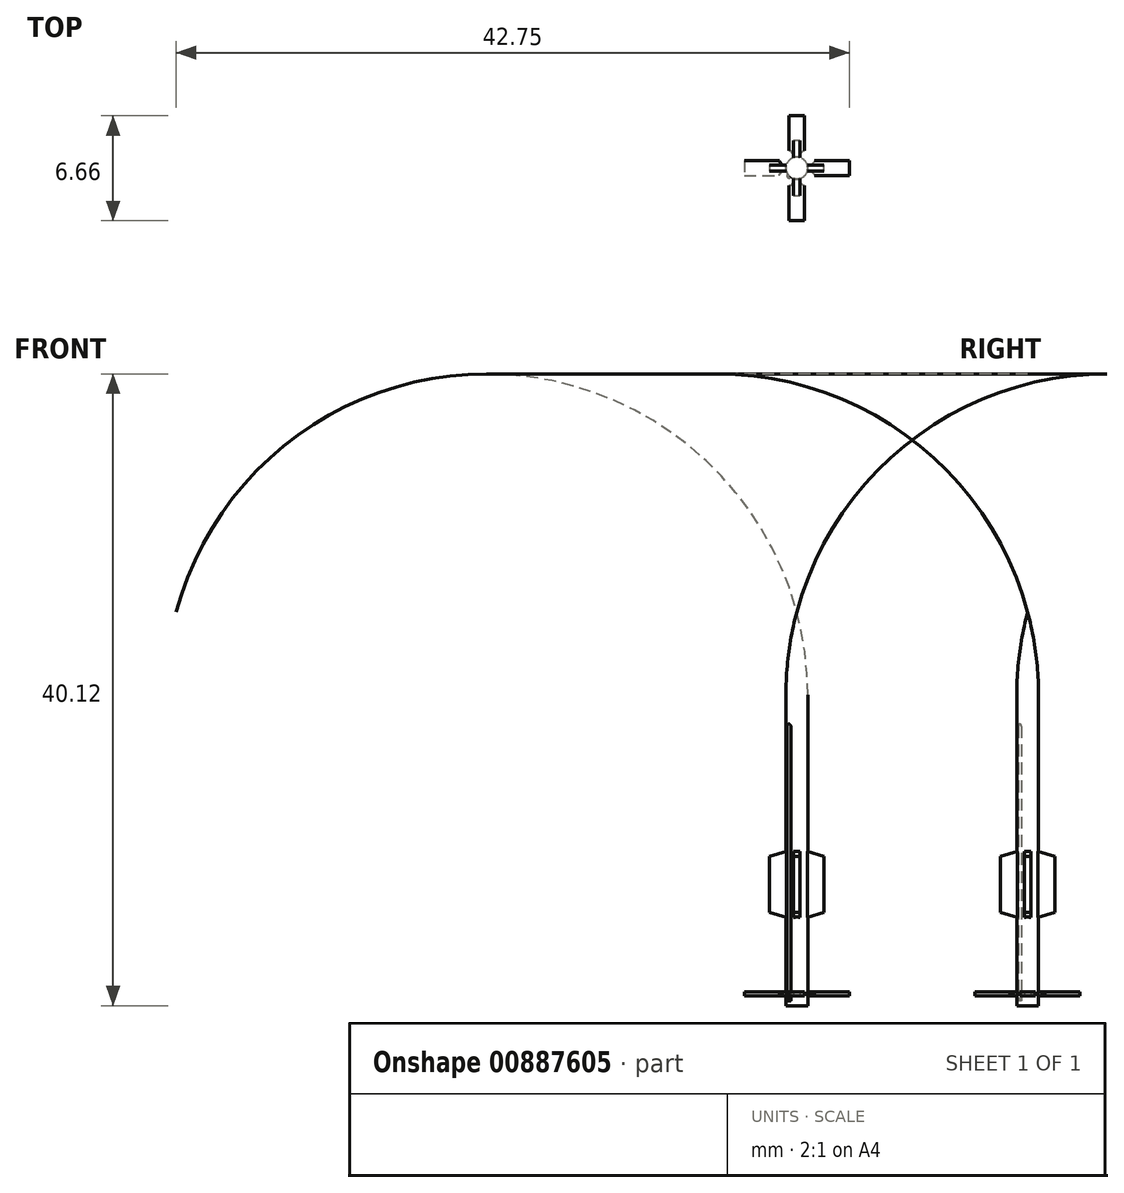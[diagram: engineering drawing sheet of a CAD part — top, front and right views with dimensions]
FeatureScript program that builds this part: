
annotation { "Feature Type Name" : "Feature", "Feature Type Description" : "" }
export const myFeature = defineFeature(function(context is Context, id is Id, definition is map)
    precondition{}
    {
        {
            assignVariable(context, id + "F0", {"name" : "s", "anyValue" : 144});
        }
        {
            var Q0;
            Q0=qCreatedBy(makeId("Front.planeOp"),FACE);
            var sketch = newSketch(context, id + "F1", { "sketchPlane" : qUnion([Q0])});
            skLineSegment(sketch, "E0", {"start": v(0, 0) * mm, "end": v(0, 25) * mm});
            skLineSegment(sketch, "E1", {"start": v(0.7, 19.72) * mm, "end": v(0.7, 0) * mm});
            skLineSegment(sketch, "E2", {"start": v(0.7, 0) * mm, "end": v(0, 0) * mm});
            skArc(sketch, "E3", {"start": v(0.7, 19.72) * mm, "mid": v(0.52, 22.38) * mm, "end": v(0, 25) * mm});
            skSolve(sketch);
        }
        {
            var Q0;
            {var subQ0=sQuery(id+"F1.wireOp",EDGE,"mrwio9nY-PsAZ-Zbfy-NhIU-sYq0QVbgGXAG");Q0=makeQuery(id+"F1.imprint","IMPRINT",FACE,{"disambiguationData":[TD([[makeQuery(id+"F1.imprint","IMPRINT",EDGE,{"derivedFrom":subQ0}),-1.0]])]});}
            var Q1;
            {var subQ7=sQuery(id+"F1.wireOp",EDGE,"E0");Q1=makeQuery(id+"F1.imprint","IMPRINT",FACE,{"disambiguationData":[TD([[makeQuery(id+"F1.imprint","IMPRINT",EDGE,{"derivedFrom":subQ7}),-1.0]])]});}
            var Q2;
            Q2=sQuery(id+"F1.wireOp",EDGE,"E0");
            revolve(context, id + "F2", {"surfaceOperationType" : NewSurfaceOperationType.NEW, "entities" : qUnion([Q0, Q1]), "axis" : qUnion([Q2]), "revolveType" : RevolveType.FULL});
        }
        {
            var Q0;
            Q0=qCreatedBy(makeId("Front.planeOp"),FACE);
            var sketch = newSketch(context, id + "F3", { "sketchPlane" : qUnion([Q0])});
            skLineSegment(sketch, "E4", {"start": v(0, 0) * mm, "end": v(0, 10) * mm});
            skLineSegment(sketch, "E5", {"start": v(0.4, 5.54) * mm, "end": v(0.4, 0.87) * mm});
            skLineSegment(sketch, "E6", {"start": v(0.4, 0.87) * mm, "end": v(3.33, 0.87) * mm});
            skLineSegment(sketch, "E7", {"start": v(3.33, 0.87) * mm, "end": v(3.33, 0.63) * mm});
            skLineSegment(sketch, "E8", {"start": v(0.7, 0) * mm, "end": v(0.7, 32.87) * mm, "construction": true});
            skPoint(sketch, "E9", {"position": v(0.7, 0.87) * mm});
            skLineSegment(sketch, "E10", {"start": v(3.33, 0.63) * mm, "end": v(0, 0.62) * mm});
            skLineSegment(sketch, "E11.0", {"start": v(0.7, 0) * mm, "end": v(-0.7, 0) * mm});
            skLineSegment(sketch, "E12", {"start": v(0.4, 5.54) * mm, "end": v(1.74, 5.94) * mm});
            skLineSegment(sketch, "E13", {"start": v(1.74, 5.94) * mm, "end": v(1.74, 9.48) * mm});
            skLineSegment(sketch, "E14", {"start": v(1.74, 9.48) * mm, "end": v(0, 10) * mm});
            skPoint(sketch, "E15", {"position": v(0.7, 5.62) * mm});
            skPoint(sketch, "E16", {"position": v(0.7, 9.8) * mm});
            skSolve(sketch);
        }
        {
            var Q0;
            Q0=qSketchRegion(id+"F3",true);
            extrude(context, id + "F4", {"entities" : qUnion([Q0]), "operationType" : NewBodyOperationType.ADD, "depth" : .4 * mm, "offsetDistance" : 25 * mm, "symmetric" : true});
        }
        {
            var Q0;
            Q0=makeQuery(id+"F4.opExtrude","SWEPT_FACE",FACE,{"disambiguationData":[OSD([sQuery(id+"F3.wireOp",EDGE,"E10")])]});
            var Q1;
            Q1=makeQuery(id+"F4.opExtrude","SWEPT_FACE",FACE,{"disambiguationData":[OSD([sQuery(id+"F3.wireOp",EDGE,"E10")])]});
            var sketch = newSketch(context, id + "F5", { "sketchPlane" : qUnion([Q0, Q1])});
            skLineSegment(sketch, "E17.bottom", {"start": v(3.33, -0.49) * mm, "end": v(1.11, -0.49) * mm});
            skLineSegment(sketch, "E17.top", {"start": v(3.33, 0.49) * mm, "end": v(1.11, 0.49) * mm});
            skLineSegment(sketch, "E17.left", {"start": v(3.33, -0.49) * mm, "end": v(3.33, 0.49) * mm});
            skLineSegment(sketch, "E17.right", {"start": v(1.11, -0.49) * mm, "end": v(1.11, 0.49) * mm});
            skLineSegment(sketch, "E18", {"start": v(0, 0) * mm, "end": v(1.11, 0) * mm});
            skSolve(sketch);
        }
        {
            var Q0;
            Q0 = qSketchRegion(id + "F5", true);
            var Q1;
            Q1=makeQuery(id+"F4.opExtrude","SWEPT_FACE",FACE,{"disambiguationData":[OSD([sQuery(id+"F3.wireOp",EDGE,"E6")])]});
            extrude(context, id + "F6", {"entities" : qUnion([Q0]), "operationType" : NewBodyOperationType.ADD, "endBound" : BoundingType.UP_TO_SURFACE, "oppositeDirection" : true, "depth" : 25 * mm, "endBoundEntityFace" : qUnion([Q1]), "offsetDistance" : 25 * mm});
        }
        {
            var Q0;
            Q0=makeQuery(id+"F2.opRevolve","SWEPT_BODY",BODY,{"disambiguationData":[OSD([sQuery(id+"F1.wireOp",EDGE,"E0"),sQuery(id+"F1.wireOp",EDGE,"E1"),sQuery(id+"F1.wireOp",EDGE,"E2"),sQuery(id+"F1.wireOp",EDGE,"2EiOItwe-9FNA-eY8p-DkXH-AMy5AHyUmzZA"),sQuery(id+"F1.wireOp",EDGE,"E3")])]});
            var Q1;
            Q1=makeQuery(id+"F2.opRevolve","SWEPT_FACE",FACE,{"disambiguationData":[OSD([sQuery(id+"F1.wireOp",EDGE,"E1")])]});
            circularPattern(context, id + "F7", {"operationType" : NewBodyOperationType.ADD, "entities" : qUnion([Q0]), "axis" : qUnion([Q1]), "angle" : 360 * degree, "instanceCount" : 4, "equalSpace" : true, "computeTransformsWithoutBuiltin" : true});
        }
        {
            var Q0;
            Q0=qCreatedBy(makeId("Top.planeOp"),FACE);
            cPlane(context, id + "F8", {"entities" : qUnion([Q0]), "cplaneType" : CPlaneType.OFFSET, "offset" : (75 / getVariable(context, 's')) * mm, "width" : 150 * mm, "height" : 150 * mm});
        }
        {
            var Q0;
            Q0=qCreatedBy(id+"F8.planeOp",FACE);
            var sketch = newSketch(context, id + "F9", { "sketchPlane" : qUnion([Q0])});
            skLineSegment(sketch, "E19", {"start": v(-0.06, -0.25) * mm, "end": v(-0.25, -0.06) * mm});
            skLineSegment(sketch, "E20", {"start": v(-0.25, -0.06) * mm, "end": v(-0.59, -0.4) * mm});
            skLineSegment(sketch, "E21", {"start": v(-0.4, -0.59) * mm, "end": v(-0.06, -0.25) * mm});
            skLineSegment(sketch, "E22", {"start": v(0, -0.45) * mm, "end": v(0, 0) * mm, "construction": true});
            skLineSegment(sketch, "E23", {"start": v(0, 0) * mm, "end": v(-0.16, -0.16) * mm, "construction": true});
            skArc(sketch, "E24", {"start": v(-0.59, -0.4) * mm, "mid": v(-0.59, -0.59) * mm, "end": v(-0.4, -0.59) * mm});
            skSolve(sketch);
        }
        {
            var Q0;
            Q0=qSketchRegion(id+"F9",true);
            extrude(context, id + "F10", {"entities" : qUnion([Q0]), "operationType" : NewBodyOperationType.ADD, "depth" : (2500 / getVariable(context, 's')) * mm, "offsetDistance" : 25 * mm});
        }
        {
            var Q0;
            Q0=makeQuery(id+"F10.boolean.opBoolean","INTERSECT",EDGE,{"derivedFrom":[makeQuery(id+"F2.opRevolve","SWEPT_FACE",FACE,{"disambiguationData":[OSD([sQuery(id+"F1.wireOp",EDGE,"E1")])]}),makeQuery(id+"F10.opExtrude","CAP_FACE",FACE,{"disambiguationData":[OSD([sQuery(id+"F9.wireOp",EDGE,"E19"),sQuery(id+"F9.wireOp",EDGE,"E20"),sQuery(id+"F9.wireOp",EDGE,"E21"),sQuery(id+"F9.wireOp",EDGE,"E24")])],"isStart":true})]});
            chamfer(context, id + "F11", {"entities" : qUnion([Q0]), "width" : .2 * mm, "tangentPropagation" : true});
        }
        {
            var Q0;
            Q0=makeQuery(id+"F10.opExtrude","CAP_EDGE",EDGE,{"disambiguationData":[OSD([sQuery(id+"F9.wireOp",EDGE,"E24")])],"isStart":false});
            fillet(context, id + "F12", {"entities" : qUnion([Q0]), "radius" : (20 / getVariable(context, 's')) * mm, "tangentPropagation" : true, "allowEdgeOverflow" : false});
        }
        {
            var Q0;
            {var subQ0=sQuery(id+"F3.wireOp",EDGE,"E6");var subQ1=sQuery(id+"F3.wireOp",EDGE,"E7");var subQ2=sQuery(id+"F3.wireOp",EDGE,"E10");Q0=makeQuery(id+"F6.boolean.opBoolean","INTERSECT",EDGE,{"derivedFrom":[makeQuery(id+"F4.boolean.opBoolean","SPLIT",FACE,{"disambiguationData":[TD([makeQuery(id+"F4.opExtrude","SWEPT_FACE",FACE,{"disambiguationData":[OSD([subQ0])]})])],"derivedFrom":makeQuery(id+"F4.opExtrude","CAP_FACE",FACE,{"disambiguationData":[OSD([sQuery(id+"F3.wireOp",EDGE,"E4"),sQuery(id+"F3.wireOp",EDGE,"E5"),subQ0,subQ1,subQ2,sQuery(id+"F3.wireOp",EDGE,"E12"),sQuery(id+"F3.wireOp",EDGE,"E13"),sQuery(id+"F3.wireOp",EDGE,"E14")])],"isStart":false})}),makeQuery(id+"F6.opExtrude","SWEPT_FACE",FACE,{"disambiguationData":[OSD([sQuery(id+"F5.wireOp",EDGE,"E17.right")])]})]});}
            var Q1;
            {var subQ0=sQuery(id+"F3.wireOp",EDGE,"E6");var subQ1=sQuery(id+"F3.wireOp",EDGE,"E7");var subQ2=sQuery(id+"F3.wireOp",EDGE,"E10");Q1=makeQuery(id+"F6.boolean.opBoolean","INTERSECT",EDGE,{"derivedFrom":[makeQuery(id+"F4.boolean.opBoolean","SPLIT",FACE,{"disambiguationData":[TD([makeQuery(id+"F4.opExtrude","SWEPT_FACE",FACE,{"disambiguationData":[OSD([subQ0])]})])],"derivedFrom":makeQuery(id+"F4.opExtrude","CAP_FACE",FACE,{"disambiguationData":[OSD([sQuery(id+"F3.wireOp",EDGE,"E4"),sQuery(id+"F3.wireOp",EDGE,"E5"),subQ0,subQ1,subQ2,sQuery(id+"F3.wireOp",EDGE,"E12"),sQuery(id+"F3.wireOp",EDGE,"E13"),sQuery(id+"F3.wireOp",EDGE,"E14")])],"isStart":true})}),makeQuery(id+"F6.opExtrude","SWEPT_FACE",FACE,{"disambiguationData":[OSD([sQuery(id+"F5.wireOp",EDGE,"E17.right")])]})]});}
            var Q2;
            {var subQ0=sQuery(id+"F3.wireOp",EDGE,"E6");var subQ1=sQuery(id+"F3.wireOp",EDGE,"E7");var subQ2=sQuery(id+"F3.wireOp",EDGE,"E10");Q2=makeQuery(id+"F7.opPattern","COPY",EDGE,{"derivedFrom":makeQuery(id+"F6.boolean.opBoolean","INTERSECT",EDGE,{"derivedFrom":[makeQuery(id+"F4.boolean.opBoolean","SPLIT",FACE,{"disambiguationData":[TD([makeQuery(id+"F4.opExtrude","SWEPT_FACE",FACE,{"disambiguationData":[OSD([subQ0])]})])],"derivedFrom":makeQuery(id+"F4.opExtrude","CAP_FACE",FACE,{"disambiguationData":[OSD([sQuery(id+"F3.wireOp",EDGE,"E4"),sQuery(id+"F3.wireOp",EDGE,"E5"),subQ0,subQ1,subQ2,sQuery(id+"F3.wireOp",EDGE,"E12"),sQuery(id+"F3.wireOp",EDGE,"E13"),sQuery(id+"F3.wireOp",EDGE,"E14")])],"isStart":false})}),makeQuery(id+"F6.opExtrude","SWEPT_FACE",FACE,{"disambiguationData":[OSD([sQuery(id+"F5.wireOp",EDGE,"E17.right")])]})]}),"instanceName":"3"});}
            var Q3;
            {var subQ0=sQuery(id+"F3.wireOp",EDGE,"E6");var subQ1=sQuery(id+"F3.wireOp",EDGE,"E7");var subQ2=sQuery(id+"F3.wireOp",EDGE,"E10");Q3=makeQuery(id+"F7.opPattern","COPY",EDGE,{"derivedFrom":makeQuery(id+"F6.boolean.opBoolean","INTERSECT",EDGE,{"derivedFrom":[makeQuery(id+"F4.boolean.opBoolean","SPLIT",FACE,{"disambiguationData":[TD([makeQuery(id+"F4.opExtrude","SWEPT_FACE",FACE,{"disambiguationData":[OSD([subQ0])]})])],"derivedFrom":makeQuery(id+"F4.opExtrude","CAP_FACE",FACE,{"disambiguationData":[OSD([sQuery(id+"F3.wireOp",EDGE,"E4"),sQuery(id+"F3.wireOp",EDGE,"E5"),subQ0,subQ1,subQ2,sQuery(id+"F3.wireOp",EDGE,"E12"),sQuery(id+"F3.wireOp",EDGE,"E13"),sQuery(id+"F3.wireOp",EDGE,"E14")])],"isStart":true})}),makeQuery(id+"F6.opExtrude","SWEPT_FACE",FACE,{"disambiguationData":[OSD([sQuery(id+"F5.wireOp",EDGE,"E17.right")])]})]}),"instanceName":"3"});}
            var Q4;
            {var subQ0=sQuery(id+"F3.wireOp",EDGE,"E6");var subQ1=sQuery(id+"F3.wireOp",EDGE,"E7");var subQ2=sQuery(id+"F3.wireOp",EDGE,"E10");Q4=makeQuery(id+"F7.opPattern","COPY",EDGE,{"derivedFrom":makeQuery(id+"F6.boolean.opBoolean","INTERSECT",EDGE,{"derivedFrom":[makeQuery(id+"F4.boolean.opBoolean","SPLIT",FACE,{"disambiguationData":[TD([makeQuery(id+"F4.opExtrude","SWEPT_FACE",FACE,{"disambiguationData":[OSD([subQ0])]})])],"derivedFrom":makeQuery(id+"F4.opExtrude","CAP_FACE",FACE,{"disambiguationData":[OSD([sQuery(id+"F3.wireOp",EDGE,"E4"),sQuery(id+"F3.wireOp",EDGE,"E5"),subQ0,subQ1,subQ2,sQuery(id+"F3.wireOp",EDGE,"E12"),sQuery(id+"F3.wireOp",EDGE,"E13"),sQuery(id+"F3.wireOp",EDGE,"E14")])],"isStart":false})}),makeQuery(id+"F6.opExtrude","SWEPT_FACE",FACE,{"disambiguationData":[OSD([sQuery(id+"F5.wireOp",EDGE,"E17.right")])]})]}),"instanceName":"2"});}
            var Q5;
            {var subQ0=sQuery(id+"F3.wireOp",EDGE,"E6");var subQ1=sQuery(id+"F3.wireOp",EDGE,"E7");var subQ2=sQuery(id+"F3.wireOp",EDGE,"E10");Q5=makeQuery(id+"F7.opPattern","COPY",EDGE,{"derivedFrom":makeQuery(id+"F6.boolean.opBoolean","INTERSECT",EDGE,{"derivedFrom":[makeQuery(id+"F4.boolean.opBoolean","SPLIT",FACE,{"disambiguationData":[TD([makeQuery(id+"F4.opExtrude","SWEPT_FACE",FACE,{"disambiguationData":[OSD([subQ0])]})])],"derivedFrom":makeQuery(id+"F4.opExtrude","CAP_FACE",FACE,{"disambiguationData":[OSD([sQuery(id+"F3.wireOp",EDGE,"E4"),sQuery(id+"F3.wireOp",EDGE,"E5"),subQ0,subQ1,subQ2,sQuery(id+"F3.wireOp",EDGE,"E12"),sQuery(id+"F3.wireOp",EDGE,"E13"),sQuery(id+"F3.wireOp",EDGE,"E14")])],"isStart":true})}),makeQuery(id+"F6.opExtrude","SWEPT_FACE",FACE,{"disambiguationData":[OSD([sQuery(id+"F5.wireOp",EDGE,"E17.right")])]})]}),"instanceName":"1"});}
            var Q6;
            {var subQ0=sQuery(id+"F3.wireOp",EDGE,"E6");var subQ1=sQuery(id+"F3.wireOp",EDGE,"E7");var subQ2=sQuery(id+"F3.wireOp",EDGE,"E10");Q6=makeQuery(id+"F7.opPattern","COPY",EDGE,{"derivedFrom":makeQuery(id+"F6.boolean.opBoolean","INTERSECT",EDGE,{"derivedFrom":[makeQuery(id+"F4.boolean.opBoolean","SPLIT",FACE,{"disambiguationData":[TD([makeQuery(id+"F4.opExtrude","SWEPT_FACE",FACE,{"disambiguationData":[OSD([subQ0])]})])],"derivedFrom":makeQuery(id+"F4.opExtrude","CAP_FACE",FACE,{"disambiguationData":[OSD([sQuery(id+"F3.wireOp",EDGE,"E4"),sQuery(id+"F3.wireOp",EDGE,"E5"),subQ0,subQ1,subQ2,sQuery(id+"F3.wireOp",EDGE,"E12"),sQuery(id+"F3.wireOp",EDGE,"E13"),sQuery(id+"F3.wireOp",EDGE,"E14")])],"isStart":false})}),makeQuery(id+"F6.opExtrude","SWEPT_FACE",FACE,{"disambiguationData":[OSD([sQuery(id+"F5.wireOp",EDGE,"E17.right")])]})]}),"instanceName":"1"});}
            var Q7;
            {var subQ0=sQuery(id+"F3.wireOp",EDGE,"E6");var subQ1=sQuery(id+"F3.wireOp",EDGE,"E7");var subQ2=sQuery(id+"F3.wireOp",EDGE,"E10");Q7=makeQuery(id+"F7.opPattern","COPY",EDGE,{"derivedFrom":makeQuery(id+"F6.boolean.opBoolean","INTERSECT",EDGE,{"derivedFrom":[makeQuery(id+"F4.boolean.opBoolean","SPLIT",FACE,{"disambiguationData":[TD([makeQuery(id+"F4.opExtrude","SWEPT_FACE",FACE,{"disambiguationData":[OSD([subQ0])]})])],"derivedFrom":makeQuery(id+"F4.opExtrude","CAP_FACE",FACE,{"disambiguationData":[OSD([sQuery(id+"F3.wireOp",EDGE,"E4"),sQuery(id+"F3.wireOp",EDGE,"E5"),subQ0,subQ1,subQ2,sQuery(id+"F3.wireOp",EDGE,"E12"),sQuery(id+"F3.wireOp",EDGE,"E13"),sQuery(id+"F3.wireOp",EDGE,"E14")])],"isStart":true})}),makeQuery(id+"F6.opExtrude","SWEPT_FACE",FACE,{"disambiguationData":[OSD([sQuery(id+"F5.wireOp",EDGE,"E17.right")])]})]}),"instanceName":"2"});}
            chamfer(context, id + "F13", {"entities" : qUnion([Q0, Q1, Q2, Q3, Q4, Q5, Q6, Q7]), "width" : (30 / getVariable(context, 's')) * mm, "tangentPropagation" : true});
        }
    });
